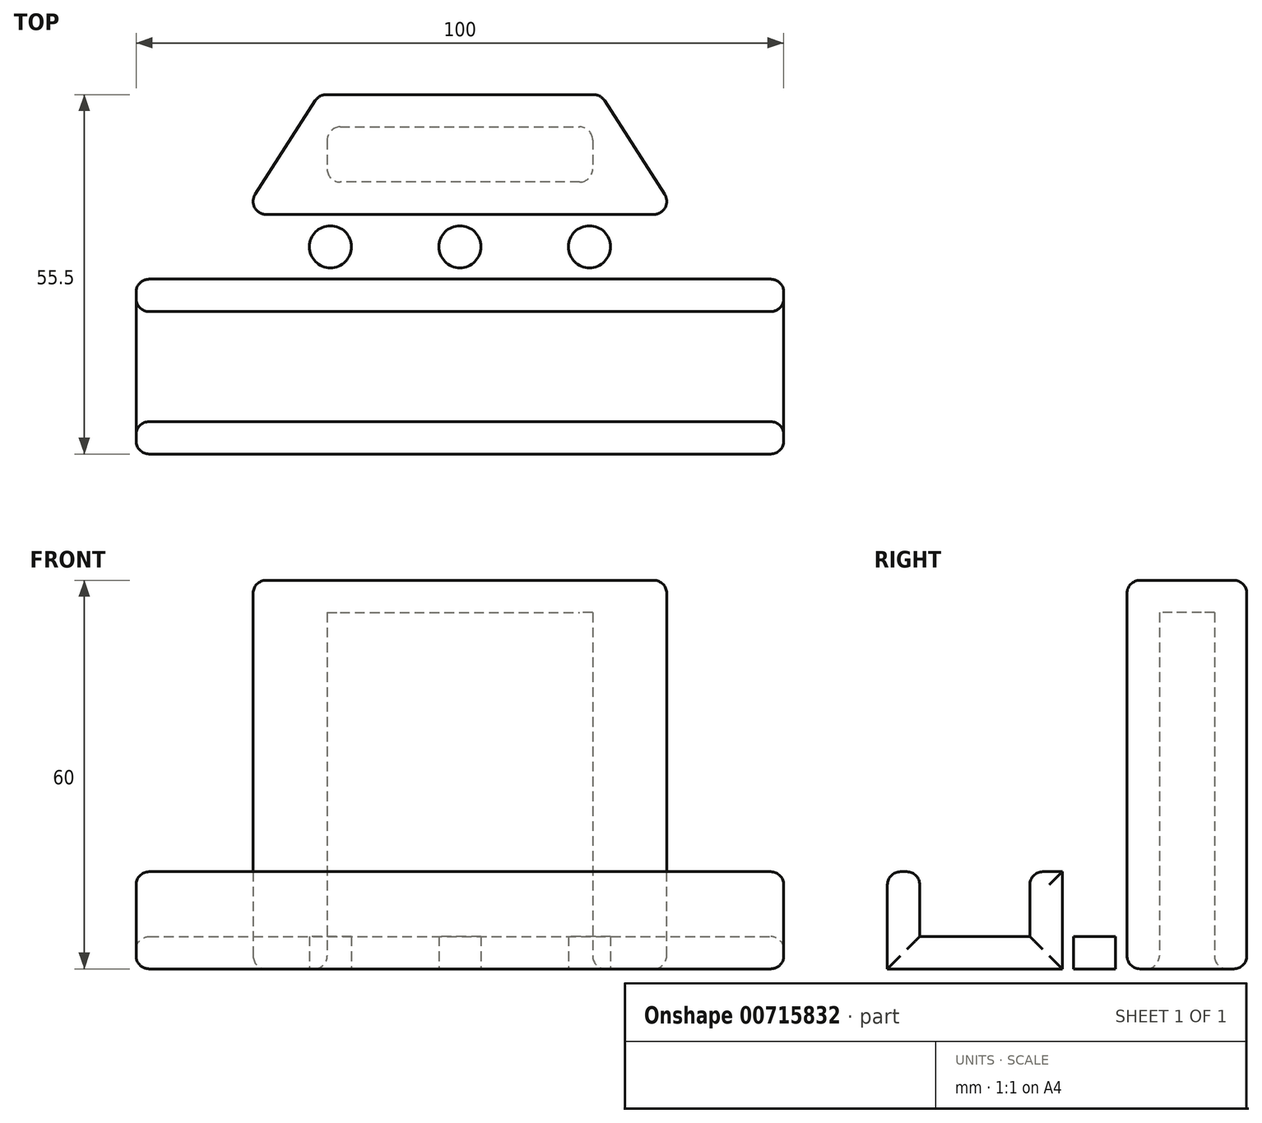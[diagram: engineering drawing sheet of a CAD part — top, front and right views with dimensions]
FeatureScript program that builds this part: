
annotation { "Feature Type Name" : "Feature", "Feature Type Description" : "" }
export const myFeature = defineFeature(function(context is Context, id is Id, definition is map)
    precondition{}
    {
        {
            var Q0;
            Q0=qCreatedBy(makeId("Top.planeOp"),FACE);
            var sketch = newSketch(context, id + "F0", { "sketchPlane" : qUnion([Q0])});
            skLineSegment(sketch, "E0.bottom", {"start": v(-50, 13.5) * mm, "end": v(50, 13.5) * mm});
            skLineSegment(sketch, "E0.top", {"start": v(-50, -13.5) * mm, "end": v(50, -13.5) * mm});
            skLineSegment(sketch, "E0.left", {"start": v(-50, 13.5) * mm, "end": v(-50, -13.5) * mm});
            skLineSegment(sketch, "E0.right", {"start": v(50, 13.5) * mm, "end": v(50, -13.5) * mm});
            skPoint(sketch, "E0.middle", {"position": v(0, 0) * mm});
            skPoint(sketch, "E1", {"position": v(0, 13.5) * mm});
            skPoint(sketch, "E2", {"position": v(-40, 13.5) * mm});
            skPoint(sketch, "E3", {"position": v(40, 13.5) * mm});
            skPoint(sketch, "E4", {"position": v(-20, 13.5) * mm});
            skPoint(sketch, "E5", {"position": v(20, 13.5) * mm});
            skPoint(sketch, "E6", {"position": v(-20, 42) * mm});
            skPoint(sketch, "E7", {"position": v(20, 42) * mm});
            skPoint(sketch, "E8", {"position": v(21.73, 42) * mm});
            skPoint(sketch, "E9", {"position": v(-21.73, 42) * mm});
            skLineSegment(sketch, "E10", {"start": v(-21.73, 42) * mm, "end": v(21.73, 42) * mm});
            skLineSegment(sketch, "E11", {"start": v(-21.73, 42) * mm, "end": v(-40, 13.5) * mm});
            skLineSegment(sketch, "E12", {"start": v(21.73, 42) * mm, "end": v(40, 13.5) * mm});
            skPoint(sketch, "E13", {"position": v(50, -8.5) * mm});
            skPoint(sketch, "E14", {"position": v(-50, -8.5) * mm});
            skPoint(sketch, "E15", {"position": v(50, 8.5) * mm});
            skPoint(sketch, "E16", {"position": v(-50, 8.5) * mm});
            skLineSegment(sketch, "E17", {"start": v(-50, 8.5) * mm, "end": v(50, 8.5) * mm});
            skLineSegment(sketch, "E18", {"start": v(50, -8.5) * mm, "end": v(-50, -8.5) * mm});
            skPoint(sketch, "E19", {"position": v(20, 23.5) * mm});
            skPoint(sketch, "E20", {"position": v(0, 23.5) * mm});
            skPoint(sketch, "E21", {"position": v(-20, 23.5) * mm});
            skPoint(sketch, "E22", {"position": v(-33.6, 23.5) * mm});
            skPoint(sketch, "E23", {"position": v(33.6, 23.5) * mm});
            skLineSegment(sketch, "E24", {"start": v(-33.6, 23.5) * mm, "end": v(33.6, 23.5) * mm});
            skPoint(sketch, "E25", {"position": v(0, 37) * mm});
            skPoint(sketch, "E25.positionSnap0", {"position": v(0, 42) * mm});
            skPoint(sketch, "E26", {"position": v(20.5, 37) * mm});
            skPoint(sketch, "E27", {"position": v(-20.5, 37) * mm});
            skPoint(sketch, "E28", {"position": v(20.5, 28.5) * mm});
            skPoint(sketch, "E29", {"position": v(-20.5, 28.5) * mm});
            skLineSegment(sketch, "E30", {"start": v(-18.5, 37) * mm, "end": v(18.5, 37) * mm});
            skLineSegment(sketch, "E31", {"start": v(20.5, 35) * mm, "end": v(20.5, 30.5) * mm});
            skLineSegment(sketch, "E32", {"start": v(18.5, 28.5) * mm, "end": v(-18.5, 28.5) * mm});
            skLineSegment(sketch, "E33", {"start": v(-20.5, 35) * mm, "end": v(-20.5, 30.5) * mm});
            skArc(sketch, "E34.filletArc", {"start": v(-18.5, 37) * mm, "mid": v(-19.91, 36.41) * mm, "end": v(-20.5, 35) * mm});
            skArc(sketch, "E35.filletArc", {"start": v(-20.5, 30.5) * mm, "mid": v(-19.91, 29.09) * mm, "end": v(-18.5, 28.5) * mm});
            skArc(sketch, "E36.filletArc", {"start": v(18.5, 28.5) * mm, "mid": v(19.91, 29.09) * mm, "end": v(20.5, 30.5) * mm});
            skArc(sketch, "E37.filletArc", {"start": v(20.5, 35) * mm, "mid": v(19.91, 36.41) * mm, "end": v(18.5, 37) * mm});
            skPoint(sketch, "E38", {"position": v(-20, 18.5) * mm});
            skPoint(sketch, "E39", {"position": v(0, 18.5) * mm});
            skPoint(sketch, "E40", {"position": v(20, 18.5) * mm});
            skCircle(sketch, "E41", {"center": v(-20, 18.5) * mm, "radius": 3.25 * mm});
            skCircle(sketch, "E42", {"center": v(0, 18.5) * mm, "radius": 3.25 * mm});
            skCircle(sketch, "E43", {"center": v(20, 18.5) * mm, "radius": 3.25 * mm});
            skSolve(sketch);
        }
        {
            var Q0;
            {var subQ0=sQuery(id+"F0.wireOp",EDGE,"E10");Q0=makeQuery(id+"F0.imprint","IMPRINT",FACE,{"disambiguationData":[TD([[makeQuery(id+"F0.imprint","IMPRINT",EDGE,{"derivedFrom":subQ0}),-1.0]])]});}
            var Q1;
            {var subQ3=sQuery(id+"F0.wireOp",EDGE,"E24");Q1=makeQuery(id+"F0.imprint","IMPRINT",FACE,{"disambiguationData":[TD([[makeQuery(id+"F0.imprint","IMPRINT",EDGE,{"derivedFrom":subQ3}),-1.0]])]});}
            var Q2;
            Q2=makeQuery(id+"F0.imprint","IMPRINT",FACE,{"disambiguationData":[TD([[makeQuery(id+"F0.imprint","IMPRINT",EDGE,{"derivedFrom":sQuery(id+"F0.wireOp",EDGE,"E41")}),1.0]])]});
            var Q3;
            Q3=makeQuery(id+"F0.imprint","IMPRINT",FACE,{"disambiguationData":[TD([[makeQuery(id+"F0.imprint","IMPRINT",EDGE,{"derivedFrom":sQuery(id+"F0.wireOp",EDGE,"E42")}),1.0]])]});
            var Q4;
            Q4=makeQuery(id+"F0.imprint","IMPRINT",FACE,{"disambiguationData":[TD([[makeQuery(id+"F0.imprint","IMPRINT",EDGE,{"derivedFrom":sQuery(id+"F0.wireOp",EDGE,"E43")}),1.0]])]});
            var Q5;
            {var subQ3=sQuery(id+"F0.wireOp",EDGE,"E17");Q5=makeQuery(id+"F0.imprint","IMPRINT",FACE,{"disambiguationData":[TD([[makeQuery(id+"F0.imprint","IMPRINT",EDGE,{"derivedFrom":subQ3}),1.0]])]});}
            var Q6;
            {var subQ0=sQuery(id+"F0.wireOp",EDGE,"E17");Q6=makeQuery(id+"F0.imprint","IMPRINT",FACE,{"disambiguationData":[TD([[makeQuery(id+"F0.imprint","IMPRINT",EDGE,{"derivedFrom":subQ0}),-1.0]])]});}
            var Q7;
            {var subQ0=sQuery(id+"F0.wireOp",EDGE,"E0.top");Q7=makeQuery(id+"F0.imprint","IMPRINT",FACE,{"disambiguationData":[TD([[makeQuery(id+"F0.imprint","IMPRINT",EDGE,{"derivedFrom":subQ0}),1.0]])]});}
            extrude(context, id + "F1", {"entities" : qUnion([Q0, Q1, Q2, Q3, Q4, Q5, Q6, Q7]), "depth" : 5 * mm, "offsetDistance" : 25 * mm});
        }
        {
            var Q0;
            {var subQ3=sQuery(id+"F0.wireOp",EDGE,"E24");Q0=makeQuery(id+"F0.imprint","IMPRINT",FACE,{"disambiguationData":[TD([[makeQuery(id+"F0.imprint","IMPRINT",EDGE,{"derivedFrom":subQ3}),-1.0]])]});}
            var Q1;
            {var subQ3=sQuery(id+"F0.wireOp",EDGE,"E17");Q1=makeQuery(id+"F0.imprint","IMPRINT",FACE,{"disambiguationData":[TD([[makeQuery(id+"F0.imprint","IMPRINT",EDGE,{"derivedFrom":subQ3}),1.0]])]});}
            var Q2;
            {var subQ0=sQuery(id+"F0.wireOp",EDGE,"E0.top");Q2=makeQuery(id+"F0.imprint","IMPRINT",FACE,{"disambiguationData":[TD([[makeQuery(id+"F0.imprint","IMPRINT",EDGE,{"derivedFrom":subQ0}),1.0]])]});}
            extrude(context, id + "F2", {"entities" : qUnion([Q0, Q1, Q2]), "operationType" : NewBodyOperationType.ADD, "depth" : 15 * mm, "offsetDistance" : 25 * mm});
        }
        {
            var Q0;
            {var subQ0=sQuery(id+"F0.wireOp",EDGE,"E10");Q0=makeQuery(id+"F0.imprint","IMPRINT",FACE,{"disambiguationData":[TD([[makeQuery(id+"F0.imprint","IMPRINT",EDGE,{"derivedFrom":subQ0}),-1.0]])]});}
            extrude(context, id + "F3", {"entities" : qUnion([Q0]), "operationType" : NewBodyOperationType.ADD, "depth" : 60 * mm, "offsetDistance" : 25 * mm});
        }
        {
            var Q0;
            Q0=makeQuery(id+"F0.imprint","IMPRINT",FACE,{"disambiguationData":[TD([[makeQuery(id+"F0.imprint","IMPRINT",EDGE,{"derivedFrom":sQuery(id+"F0.wireOp",EDGE,"E30")}),-1.0]])]});
            extrude(context, id + "F4", {"entities" : qUnion([Q0]), "operationType" : NewBodyOperationType.ADD, "depth" : 60 * mm, "offsetDistance" : 25 * mm, "hasSecondDirection" : true, "secondDirectionOppositeDirection" : false, "secondDirectionDepth" : 55 * mm});
        }
        {
            var Q0;
            Q0=makeQuery(id+"F1.opExtrude","CAP_FACE",FACE,{"disambiguationData":[OSD([sQuery(id+"F0.wireOp",EDGE,"E0.bottom"),sQuery(id+"F0.wireOp",EDGE,"E0.top"),sQuery(id+"F0.wireOp",EDGE,"E0.left"),sQuery(id+"F0.wireOp",EDGE,"E0.right"),sQuery(id+"F0.wireOp",EDGE,"E10"),sQuery(id+"F0.wireOp",EDGE,"E11"),sQuery(id+"F0.wireOp",EDGE,"E12"),sQuery(id+"F0.wireOp",EDGE,"E30"),sQuery(id+"F0.wireOp",EDGE,"E31"),sQuery(id+"F0.wireOp",EDGE,"E32"),sQuery(id+"F0.wireOp",EDGE,"E33"),sQuery(id+"F0.wireOp",EDGE,"E34.filletArc"),sQuery(id+"F0.wireOp",EDGE,"E35.filletArc"),sQuery(id+"F0.wireOp",EDGE,"E36.filletArc"),sQuery(id+"F0.wireOp",EDGE,"E37.filletArc")])],"isStart":true});
            var Q1;
            {var subQ0=sQuery(id+"F0.wireOp",EDGE,"E11");Q1=makeQuery(id+"F3.boolean.opBoolean","MERGE",FACE,{"derivedFrom":[makeQuery(id+"F2.boolean.opBoolean","MERGE",FACE,{"derivedFrom":[makeQuery(id+"F1.opExtrude","SWEPT_FACE",FACE,{"disambiguationData":[OSD([subQ0])]}),makeQuery(id+"F2.opExtrude","SWEPT_FACE",FACE,{"disambiguationData":[OSD([subQ0])]})]}),makeQuery(id+"F3.opExtrude","SWEPT_FACE",FACE,{"disambiguationData":[OSD([subQ0])]})]});}
            var Q2;
            {var subQ0=sQuery(id+"F0.wireOp",EDGE,"E0.left");Q2=makeQuery(id+"F2.boolean.opBoolean","MERGE",FACE,{"derivedFrom":[makeQuery(id+"F1.opExtrude","SWEPT_FACE",FACE,{"disambiguationData":[OSD([subQ0])]}),makeQuery(id+"F2.opExtrude","SWEPT_FACE",FACE,{"disambiguationData":[OSD([subQ0]),TDD([makeQuery(id+"F0.imprint","IMPRINT",EDGE,{"disambiguationData":[TD([[makeQuery(id+"F0.imprint","INTERSECT",VERTEX,{"derivedFrom":[sQuery(id+"F0.wireOp",EDGE,"E0.bottom"),subQ0]}),-1.0]])],"derivedFrom":subQ0})])]}),makeQuery(id+"F2.opExtrude","SWEPT_FACE",FACE,{"disambiguationData":[OSD([subQ0]),TDD([makeQuery(id+"F0.imprint","IMPRINT",EDGE,{"disambiguationData":[TD([[makeQuery(id+"F0.imprint","INTERSECT",VERTEX,{"derivedFrom":[sQuery(id+"F0.wireOp",EDGE,"E0.top"),subQ0]}),1.0]])],"derivedFrom":subQ0})])]})]});}
            var Q3;
            {var subQ0=sQuery(id+"F0.wireOp",EDGE,"E12");Q3=makeQuery(id+"F3.boolean.opBoolean","MERGE",FACE,{"derivedFrom":[makeQuery(id+"F2.boolean.opBoolean","MERGE",FACE,{"derivedFrom":[makeQuery(id+"F1.opExtrude","SWEPT_FACE",FACE,{"disambiguationData":[OSD([subQ0])]}),makeQuery(id+"F2.opExtrude","SWEPT_FACE",FACE,{"disambiguationData":[OSD([subQ0])]})]}),makeQuery(id+"F3.opExtrude","SWEPT_FACE",FACE,{"disambiguationData":[OSD([subQ0])]})]});}
            var Q4;
            {var subQ0=sQuery(id+"F0.wireOp",EDGE,"E0.right");Q4=makeQuery(id+"F2.boolean.opBoolean","MERGE",FACE,{"derivedFrom":[makeQuery(id+"F1.opExtrude","SWEPT_FACE",FACE,{"disambiguationData":[OSD([subQ0])]}),makeQuery(id+"F2.opExtrude","SWEPT_FACE",FACE,{"disambiguationData":[OSD([subQ0]),TDD([makeQuery(id+"F0.imprint","IMPRINT",EDGE,{"disambiguationData":[TD([[makeQuery(id+"F0.imprint","INTERSECT",VERTEX,{"derivedFrom":[sQuery(id+"F0.wireOp",EDGE,"E0.bottom"),subQ0]}),-1.0]])],"derivedFrom":subQ0})])]}),makeQuery(id+"F2.opExtrude","SWEPT_FACE",FACE,{"disambiguationData":[OSD([subQ0]),TDD([makeQuery(id+"F0.imprint","IMPRINT",EDGE,{"disambiguationData":[TD([[makeQuery(id+"F0.imprint","INTERSECT",VERTEX,{"derivedFrom":[sQuery(id+"F0.wireOp",EDGE,"E0.top"),subQ0]}),1.0]])],"derivedFrom":subQ0})])]})]});}
            var Q5;
            {var subQ0=sQuery(id+"F0.wireOp",EDGE,"E37.filletArc");var subQ1=sQuery(id+"F0.wireOp",EDGE,"E36.filletArc");var subQ2=sQuery(id+"F0.wireOp",EDGE,"E35.filletArc");var subQ3=sQuery(id+"F0.wireOp",EDGE,"E34.filletArc");var subQ4=sQuery(id+"F0.wireOp",EDGE,"E33");var subQ5=sQuery(id+"F0.wireOp",EDGE,"E32");var subQ6=sQuery(id+"F0.wireOp",EDGE,"E31");var subQ7=sQuery(id+"F0.wireOp",EDGE,"E30");Q5=makeQuery(id+"F4.boolean.opBoolean","MERGE",FACE,{"derivedFrom":[makeQuery(id+"F3.opExtrude","CAP_FACE",FACE,{"disambiguationData":[OSD([sQuery(id+"F0.wireOp",EDGE,"E10"),sQuery(id+"F0.wireOp",EDGE,"E11"),sQuery(id+"F0.wireOp",EDGE,"E12"),sQuery(id+"F0.wireOp",EDGE,"E24"),subQ7,subQ6,subQ5,subQ4,subQ3,subQ2,subQ1,subQ0])],"isStart":false}),makeQuery(id+"F4.opExtrude","CAP_FACE",FACE,{"disambiguationData":[OSD([subQ7,subQ6,subQ5,subQ4,subQ3,subQ2,subQ1,subQ0])],"isStart":false})]});}
            var Q6;
            Q6=makeQuery(id+"F2.opExtrude","CAP_FACE",FACE,{"disambiguationData":[OSD([sQuery(id+"F0.wireOp",EDGE,"E0.top"),sQuery(id+"F0.wireOp",EDGE,"E0.left"),sQuery(id+"F0.wireOp",EDGE,"E0.right"),sQuery(id+"F0.wireOp",EDGE,"E18")])],"isStart":false});
            var Q7;
            Q7=makeQuery(id+"F2.opExtrude","CAP_EDGE",EDGE,{"disambiguationData":[OSD([sQuery(id+"F0.wireOp",EDGE,"E17")])],"isStart":false});
            fillet(context, id + "F5", {"entities" : qUnion([Q0, Q1, Q2, Q3, Q4, Q5, Q6, Q7]), "radius" : 2 * mm, "tangentPropagation" : true, "allowEdgeOverflow" : false});
        }
    });
